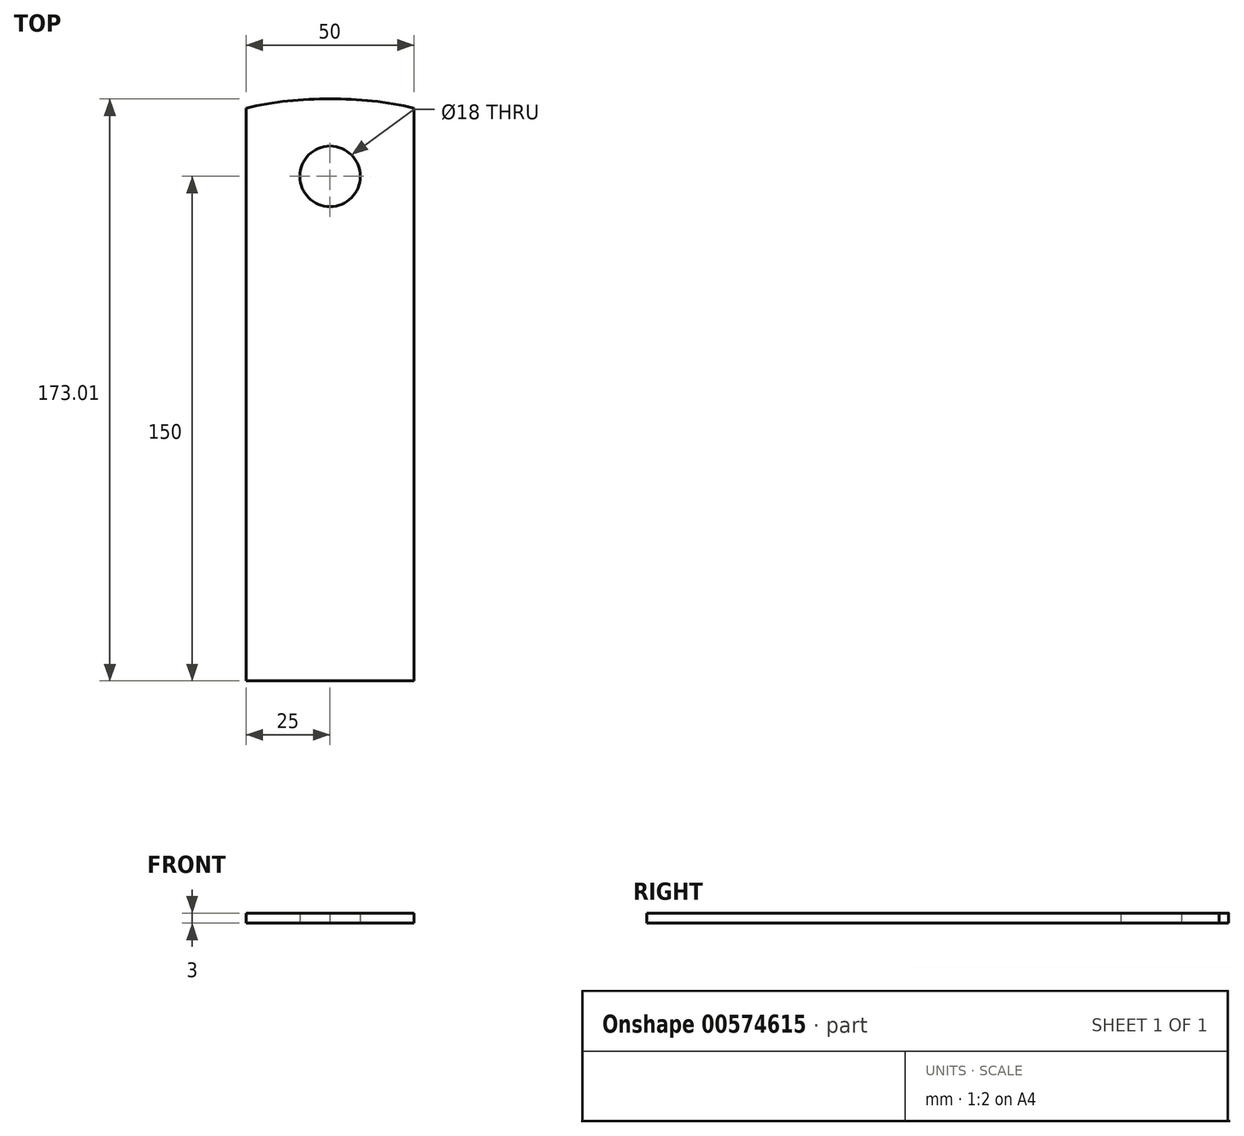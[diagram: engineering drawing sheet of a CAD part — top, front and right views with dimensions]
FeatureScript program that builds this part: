
annotation { "Feature Type Name" : "Feature", "Feature Type Description" : "" }
export const myFeature = defineFeature(function(context is Context, id is Id, definition is map)
    precondition{}
    {
        {
            var Q0;
            Q0=qCreatedBy(makeId("Top.planeOp"),FACE);
            var sketch = newSketch(context, id + "F0", { "sketchPlane" : qUnion([Q0])});
            skLineSegment(sketch, "E0.bottom", {"start": v(0, 0) * mm, "end": v(50, 0) * mm});
            skLineSegment(sketch, "E0.left", {"start": v(0, 0) * mm, "end": v(0, 170.26) * mm});
            skLineSegment(sketch, "E0.right", {"start": v(50, 0) * mm, "end": v(50, 170.26) * mm});
            skCircle(sketch, "E1", {"center": v(25, 150) * mm, "radius": 9 * mm});
            skArc(sketch, "E2", {"start": v(25, 173) * mm, "mid": v(37.58, 172.39) * mm, "end": v(50, 170.26) * mm});
            skArc(sketch, "E3.MirrorCS", {"start": v(25, 173) * mm, "mid": v(12.42, 172.39) * mm, "end": v(0, 170.26) * mm});
            skSolve(sketch);
        }
        {
            var Q0;
            Q0=makeQuery(id+"F0.imprint","IMPRINT",FACE,{"disambiguationData":[TD([[makeQuery(id+"F0.imprint","IMPRINT",EDGE,{"derivedFrom":sQuery(id+"F0.wireOp",EDGE,"E0.bottom")}),1.0]])]});
            extrude(context, id + "F1", {"entities" : qUnion([Q0]), "depth" : 3 * mm, "offsetDistance" : 25 * mm});
        }
    });
